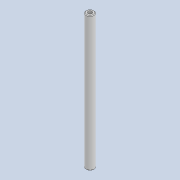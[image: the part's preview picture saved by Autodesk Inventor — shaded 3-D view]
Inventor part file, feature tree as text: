
AUTODESK INVENTOR PART (.ipt)
format: ipt  version: 2020 (Build 240168000, 168)  size: 79,360 bytes
history: native  units: mm
features: extrude x1, chamfer x1, sketch x1
ambient origin geometry x8: Origin, YZ Plane, XZ Plane, XY Plane, X Axis, Y Axis, Z Axis, Center Point
bodies: Solid1 (feature_tree)
feature tree (3):
  extrude  "Extrusion1"  Depth=1.5mm
  chamfer  "Chamfer1"  Distance=50.0mm
  sketch  "Sketch1"  dims[d0=3.0mm d1=1.5mm d2=50.0mm d3=0.0mm d4=0.25mm d5=2.0mm d6=45.0deg]
